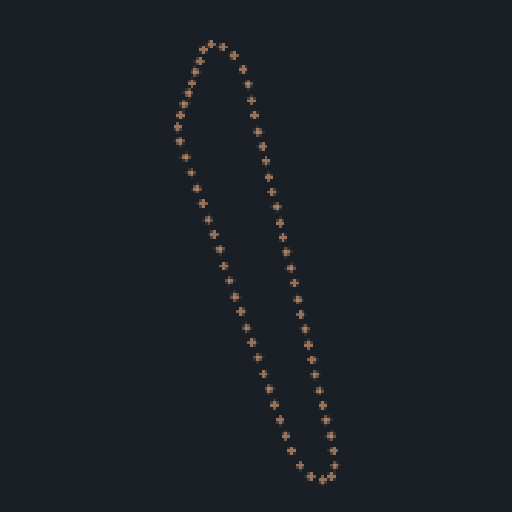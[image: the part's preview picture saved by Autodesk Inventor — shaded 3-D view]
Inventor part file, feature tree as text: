
AUTODESK INVENTOR PART (.ipt)
format: ipt  version: 2025 (Build 290162000, 162)  size: 95,232 bytes
history: native  units: in
note: dims shown in document units (in); Inventor stores cm internally (conversion verified against a paired STEP export)
features: other x69, reference x6, sketch x1, pattern_linear x1
ambient origin geometry x8: Origin, YZ Plane, XZ Plane, XY Plane, X Axis, Y Axis, Z Axis, Center Point
feature tree (77):
  sketch  "Sketch1"  dims[d0=24.6604in]
  other  "Work Point3"
  pattern_linear  "Rectangular Pattern1"  [2 undecoded]
  reference  "Reference1"
  reference  "Reference2"
  reference  "Reference3"
  reference  "Reference4"
  reference  "Reference5"
  reference  "Reference6"
  other  "Work Point4"
  other  "Work Point5"
  other  "Work Point6"
  other  "Work Point7"
  other  "Work Point8"
  other  "Work Point9"
  other  "Work Point10"
  other  "Work Point11"
  other  "Work Point12"
  other  "Work Point13"
  other  "Work Point14"
  other  "Work Point15"
  other  "Work Point16"
  other  "Work Point17"
  other  "Work Point18"
  other  "Work Point19"
  other  "Work Point20"
  other  "Work Point21"
  other  "Work Point22"
  other  "Work Point23"
  other  "Work Point24"
  other  "Work Point25"
  other  "Work Point26"
  other  "Work Point27"
  other  "Work Point28"
  other  "Work Point29"
  other  "Work Point30"
  other  "Work Point31"
  other  "Work Point32"
  other  "Work Point33"
  other  "Work Point34"
  other  "Work Point35"
  other  "Work Point36"
  other  "Work Point37"
  other  "Work Point38"
  other  "Work Point39"
  other  "Work Point40"
  other  "Work Point41"
  other  "Work Point42"
  other  "Work Point43"
  other  "Work Point44"
  other  "Work Point45"
  other  "Work Point46"
  other  "Work Point47"
  other  "Work Point48"
  other  "Work Point49"
  other  "Work Point50"
  other  "Work Point51"
  other  "Work Point52"
  other  "Work Point53"
  other  "Work Point54"
  other  "Work Point55"
  other  "Work Point56"
  other  "Work Point57"
  other  "Work Point58"
  other  "Work Point59"
  other  "Work Point60"
  other  "Work Point61"
  other  "Work Point62"
  other  "Work Point63"
  other  "Work Point64"
  other  "Work Point65"
  parser-record x1  (decoder bookkeeping rows leaked as tree rows — omitted from the tree; the rows remain in map.json)
  other  "!tower.iam"
  other  "9P 12T Sprocket, No Insert:2"
  other  "12T"
  other  "9P 12T Sprocket, No Insert:4"
  other  "9P 12T Sprocket, No Insert:3"
note: 2 required parameter values undecoded (feature->parameter linkage not recoverable at this tier; creation-order binding heuristic only, values carry confidence <= 0.55)
note: 1 file-system path scrubbed to <path> (originals preserved in map.json)
